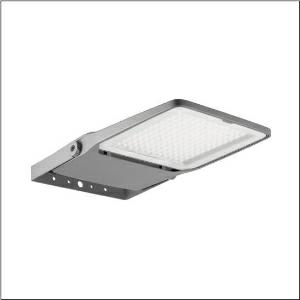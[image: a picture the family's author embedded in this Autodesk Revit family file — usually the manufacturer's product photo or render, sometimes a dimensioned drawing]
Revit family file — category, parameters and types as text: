
# Revit family: floodlight_fl_20_midi___rs17_5xa7682d2b2ac_2315
name_source: partatom
category: Lighting Fixtures
units: mm (PartAtom-declared; Revit-internal decimal feet)

## family parameters
Cut with Voids When Loaded = No
Host = Face
Light Source = No
Part Type = Normal
Room Calculation Point = No
Round Connector Dimension = Use Diameter
Shared = No

## types (1)
- --- (1 x LED 4000K / CRI = 70 (unbekannt), 19540 lm, 4000K)
    Apparent Load = 142 VA
    CIE Flux Codes = 79 92 99 100 100
    Color Rendering = 70
    Color Temperature = 4000K
    Default Elevation = 1800 mm
    Description = Floodlight FL 20 midi, floodlight, primary light control with lens, of plastic, primary optical cover: protective disc, of toughened safety glass, transparent, light distribution: RS17, light emission: direct distribution, primary light characteristic: rotationally symmetric, installation type: surface-mounted, LED High Power LED, rated luminous flux: 19.540 lm, light colour: 740, colour temperature: 4000K, control gear: ECG Plus, control: flexible luminous flux parameterisation, time-dependent luminous flux control, digital communication interface, power reduction, overheat protection, electronic power reduction, with terminal, 5-pole, max. 2.5mm², mains connection: 220..240V, AC, 50/60Hz, rated input power: 142W, LED unit, of diecast aluminium, powder-coated, Siteco® metallic grey (DB 702S), length: 731 mm, width: 450 mm, height: 76mm, housing frame, of diecast aluminium, powder-coated, Siteco® metallic grey (DB 702S), wall fastening, of steel, powder-coated, Siteco® metallic grey (DB 702S), DALIprotection rating (complete): IP66, insulation class (complete): insulation class II (safety insulation), certification: CE, ENEC, VDE, protection symbol: D, permissible ambient temperature for indoor applications: -40..+40°C, permissible ambient temperature for outdoor applications: -40..+50°C, standard: DIN EN 12944, packaging unit: 1 piece

Light Distribution: RS17
    Height = 76 mm
    Lamp = 1 x LED 4000K / CRI >= 70 (unbekannt)
    Lamp Light Flux = 19540 lm
    Lamp count = 1
    Length = 731 mm
    Luminous efficacy = 138 lm/W
    Manufacturer = Siteco
    ModVariant = No
    Model = 5XA7682D2B2AC
    Number of Poles = 1
    OnlyDefault = Yes
    Power Factor = 1
    Product Name = Floodlight FL 20 midi | RS17
    Product group = floodlight | pylon top
    ProductGroupID = 6101
    Protection Class = Protection class II
    Protection Degree = IP 66
    RLX_Detail_Level = 1
    RlxData = <blob elided: 86309 chars, md5=d83f0385>
    Socket = socket
    Standby Power = 0 W
    System Light Flux = 19540 lm
    System Power = 142 W
    Type Comments = factory setting: luminous flux: 100 % | dim-lin: 254 | 489 mA
    Type Image = l_1005944.jpg
    URL = http://relux.com
    VarID = @adj_141993
    Voltage = 0 V
    Weight = 0.00 kg
    Width = 450 mm

## geometry (parser evidence)
native form markers: Blend x4, Sweep x14
no freeform markers — native parametric forms only
